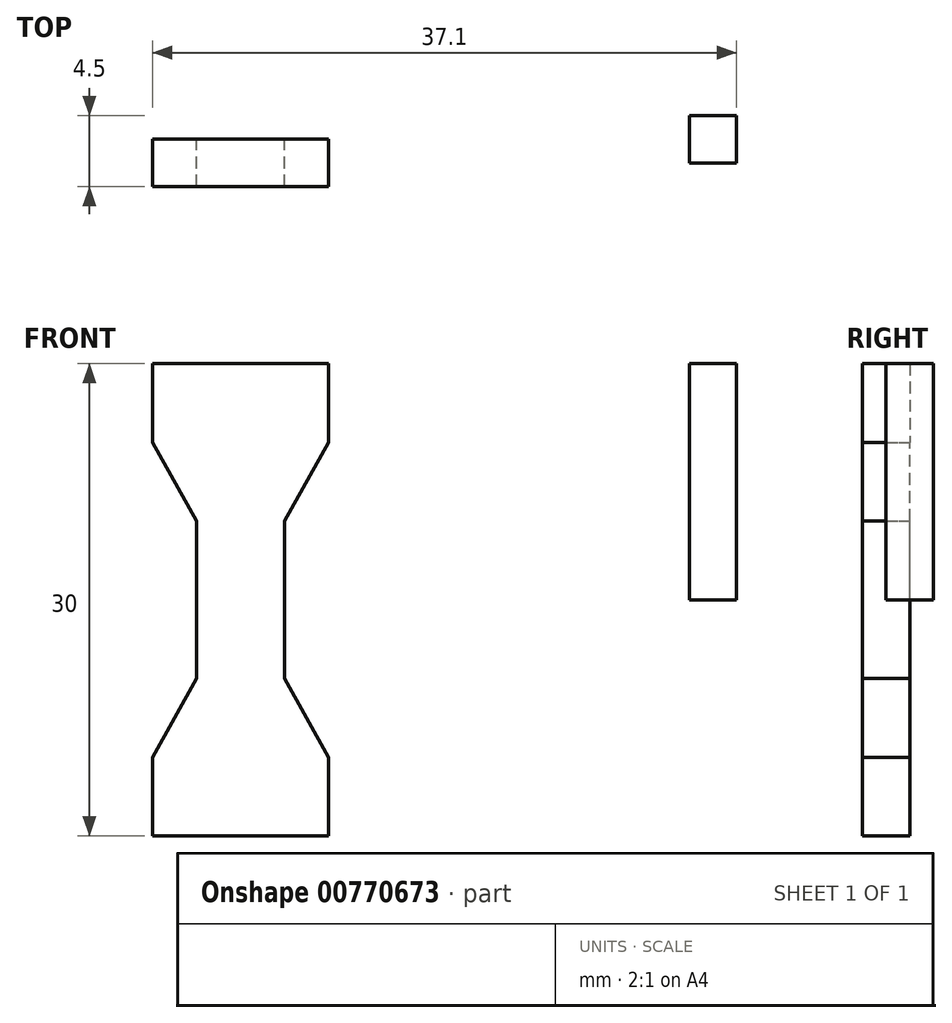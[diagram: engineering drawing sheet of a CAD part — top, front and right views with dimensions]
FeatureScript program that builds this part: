
annotation { "Feature Type Name" : "Feature", "Feature Type Description" : "" }
export const myFeature = defineFeature(function(context is Context, id is Id, definition is map)
    precondition{}
    {
        {
            var Q0;
            Q0=qCreatedBy(makeId("Top.planeOp"),FACE);
            var sketch = newSketch(context, id + "F0", { "sketchPlane" : qUnion([Q0])});
            skLineSegment(sketch, "E0.bottom", {"start": v(1.5, -1.5) * mm, "end": v(-1.5, -1.5) * mm});
            skLineSegment(sketch, "E0.top", {"start": v(1.5, 1.5) * mm, "end": v(-1.5, 1.5) * mm});
            skLineSegment(sketch, "E0.left", {"start": v(1.5, -1.5) * mm, "end": v(1.5, 1.5) * mm});
            skLineSegment(sketch, "E0.right", {"start": v(-1.5, -1.5) * mm, "end": v(-1.5, 1.5) * mm});
            skPoint(sketch, "E0.middle", {"position": v(0, 0) * mm});
            skSolve(sketch);
        }
        {
            var Q0;
            Q0 = qSketchRegion(id + "F0", true);
            extrude(context, id + "F1", {"entities" : qUnion([Q0]), "depth" : 15 * mm, "offsetDistance" : 25 * mm});
        }
        {
            var Q0;
            Q0=qCreatedBy(makeId("Front.planeOp"),FACE);
            var sketch = newSketch(context, id + "F2", { "sketchPlane" : qUnion([Q0])});
            skLineSegment(sketch, "E1.bottom", {"start": v(-24.4, -15) * mm, "end": v(-35.6, -15) * mm});
            skLineSegment(sketch, "E1.top", {"start": v(-24.4, 15) * mm, "end": v(-35.6, 15) * mm});
            skLineSegment(sketch, "E1.left", {"start": v(-24.4, -15) * mm, "end": v(-24.4, 15) * mm, "construction": true});
            skLineSegment(sketch, "E1.right", {"start": v(-35.6, -15) * mm, "end": v(-35.6, 15) * mm, "construction": true});
            skPoint(sketch, "E1.middle", {"position": v(-30, 0) * mm});
            skLineSegment(sketch, "E2.bottom", {"start": v(-27.21, -5) * mm, "end": v(-32.79, -5) * mm, "construction": true});
            skLineSegment(sketch, "E2.top", {"start": v(-27.21, 5) * mm, "end": v(-32.79, 5) * mm, "construction": true});
            skLineSegment(sketch, "E2.left", {"start": v(-27.21, -5) * mm, "end": v(-27.21, 5) * mm});
            skLineSegment(sketch, "E2.right", {"start": v(-32.79, -5) * mm, "end": v(-32.79, 5) * mm});
            skLineSegment(sketch, "E3.bottom", {"start": v(-35.6, 15) * mm, "end": v(-24.4, 15) * mm});
            skLineSegment(sketch, "E3.top", {"start": v(-35.6, 10) * mm, "end": v(-24.4, 10) * mm, "construction": true});
            skLineSegment(sketch, "E3.left", {"start": v(-35.6, 15) * mm, "end": v(-35.6, 10) * mm});
            skLineSegment(sketch, "E3.right", {"start": v(-24.4, 15) * mm, "end": v(-24.4, 10) * mm});
            skLineSegment(sketch, "E4.bottom", {"start": v(-35.6, -15) * mm, "end": v(-24.4, -15) * mm});
            skLineSegment(sketch, "E4.top", {"start": v(-35.6, -10) * mm, "end": v(-24.4, -10) * mm, "construction": true});
            skLineSegment(sketch, "E4.left", {"start": v(-35.6, -15) * mm, "end": v(-35.6, -10) * mm});
            skLineSegment(sketch, "E4.right", {"start": v(-24.4, -15) * mm, "end": v(-24.4, -10) * mm});
            skLineSegment(sketch, "E5", {"start": v(-35.6, 10) * mm, "end": v(-32.79, 5) * mm});
            skLineSegment(sketch, "E6", {"start": v(-35.6, -10) * mm, "end": v(-32.79, -5) * mm});
            skLineSegment(sketch, "E7", {"start": v(-27.21, -5) * mm, "end": v(-24.4, -10) * mm});
            skLineSegment(sketch, "E8", {"start": v(-27.21, 5) * mm, "end": v(-24.4, 10) * mm});
            skSolve(sketch);
        }
        {
            var Q0;
            Q0 = qSketchRegion(id + "F2", true);
            extrude(context, id + "F3", {"entities" : qUnion([Q0]), "depth" : 3 * mm, "offsetDistance" : 25 * mm});
        }
    });
